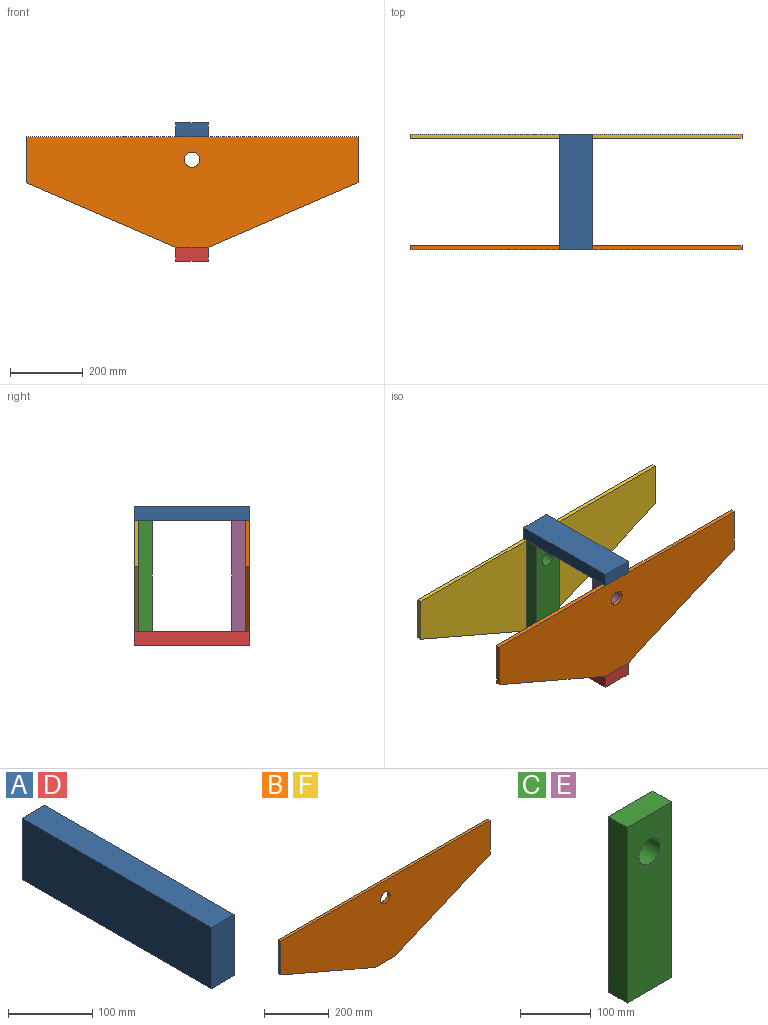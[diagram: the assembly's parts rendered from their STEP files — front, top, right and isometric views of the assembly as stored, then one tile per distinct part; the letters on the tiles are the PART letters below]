
ASSEMBLY  parts=6 mates=11
PART A: 6 faces, bbox 38.1x317.5x88.9 mm
  f0: plane 317.5x88.9mm, normal (1,0,0), area 28225.8mm2, adj f1,f3,f4,f5
  f1: plane 317.5x38.1mm, normal (0,0,1), area 12096.7mm2, adj f0,f2,f4,f5
  f2: plane 317.5x88.9mm, normal (-1,0,0), area 28225.8mm2, adj f1,f3,f4,f5
  f3: plane 317.5x38.1mm, normal (0,0,-1), area 12096.7mm2, adj f0,f2,f4,f5
  f4: plane 88.9x38.1mm, normal (0,-1,0), area 3387.1mm2, adj f0,f1,f2,f3
  f5: plane 88.9x38.1mm, normal (0,1,0), area 3387.1mm2, adj f0,f1,f2,f3
PART B: 9 faces, bbox 914.4x11.1x304.8 mm
  f0: plane 914.4x11.11mm, normal (0,0,1), area 10161.3mm2, adj f1,f6,f7,f8
  f1: plane 127x11.11mm, normal (-1,0,0), area 1411.3mm2, adj f0,f2,f7,f8
  f2: plane 412.75x177.8mm, normal (-0.4,0,-0.92), area 4994.1mm2, adj f1,f3,f7,f8
  f3: plane 88.9x11.11mm, normal (0,0,-1), area 987.9mm2, adj f2,f4,f7,f8
  f4: plane 412.75x177.8mm, normal (0.4,0,-0.92), area 4994.1mm2, adj f3,f6,f7,f8
  f5: cylinder r=21.08mm len=42.16mm, axis (0,1,0), area 1472mm2, adj f7,f8
  f6: plane 127x11.11mm, normal (1,0,0), area 1411.3mm2, adj f0,f4,f7,f8
  f7: plane 914.4x304.8mm, normal (0,-1,0), area 203925.9mm2, adj f0,f1,f2,f3,f4,f5,f6
  f8: plane 914.4x304.8mm, normal (0,1,0), area 203925.9mm2, adj f0,f1,f2,f3,f4,f5,f6
PART C: 7 faces, bbox 88.9x38.1x304.8 mm
  f0: plane 88.9x38.1mm, normal (0,0,-1), area 3387.1mm2, adj f1,f4,f5,f6
  f1: plane 304.8x38.1mm, normal (1,0,0), area 11612.9mm2, adj f0,f2,f5,f6
  f2: plane 88.9x38.1mm, normal (0,0,1), area 3387.1mm2, adj f1,f4,f5,f6
  f3: cylinder r=21.08mm len=42.16mm, axis (0,1,0), area 5046.8mm2, adj f5,f6
  f4: plane 304.8x38.1mm, normal (-1,0,0), area 11612.9mm2, adj f0,f2,f5,f6
  f5: plane 304.8x88.9mm, normal (0,-1,0), area 25700.4mm2, adj f0,f1,f2,f3,f4
  f6: plane 304.8x88.9mm, normal (0,1,0), area 25700.4mm2, adj f0,f1,f2,f3,f4
PART D: same geometry as A
PART E: same geometry as C
PART F: same geometry as B
PLACE A rot(axis=(0,1,0),90deg) t=(45.37,-125.3,-454.64)mm
PLACE B t=(-189.31,-272.94,-473.69)mm
PLACE C t=(45.37,22.34,-626.09)mm
PLACE D rot(axis=(0,1,0),90deg) t=(45.37,-125.3,-797.54)mm
PLACE E t=(45.37,-234.84,-626.09)mm
PLACE F t=(-189.31,33.45,-473.69)mm
MATE planar A.f5 <-> F.f8  axis (0,1,0) through (45.37,33.45,-454.64)mm
MATE planar A.f0 <-> F.f0  axis (0,0,-1) through (45.37,-125.3,-473.69)mm
MATE fastened C.f0 <-> F.f3  axis (0,0,1) through (0.92,22.34,-778.49)mm
MATE planar A.f4 <-> B.f7  axis (0,-1,0) through (45.37,-284.05,-454.64)mm
MATE planar A.f3 <-> E.f4  axis (-1,0,0) through (0.92,-125.3,-454.64)mm
MATE planar A.f0 <-> B.f0  axis (0,0,-1) through (45.37,-125.3,-473.69)mm
MATE planar C.f2 <-> A.f0  axis (0,0,1) through (45.37,3.29,-473.69)mm
MATE planar A.f3 <-> C.f4  axis (-1,0,0) through (0.92,-125.3,-454.64)mm
MATE fastened D.f2 <-> F.f3  axis (0,0,1) through (0.92,33.45,-778.49)mm
MATE planar E.f2 <-> A.f0  axis (0,0,1) through (45.37,-253.89,-473.69)mm
MATE fastened E.f0 <-> B.f3  axis (0,0,-1) through (0.92,-272.94,-778.49)mm
